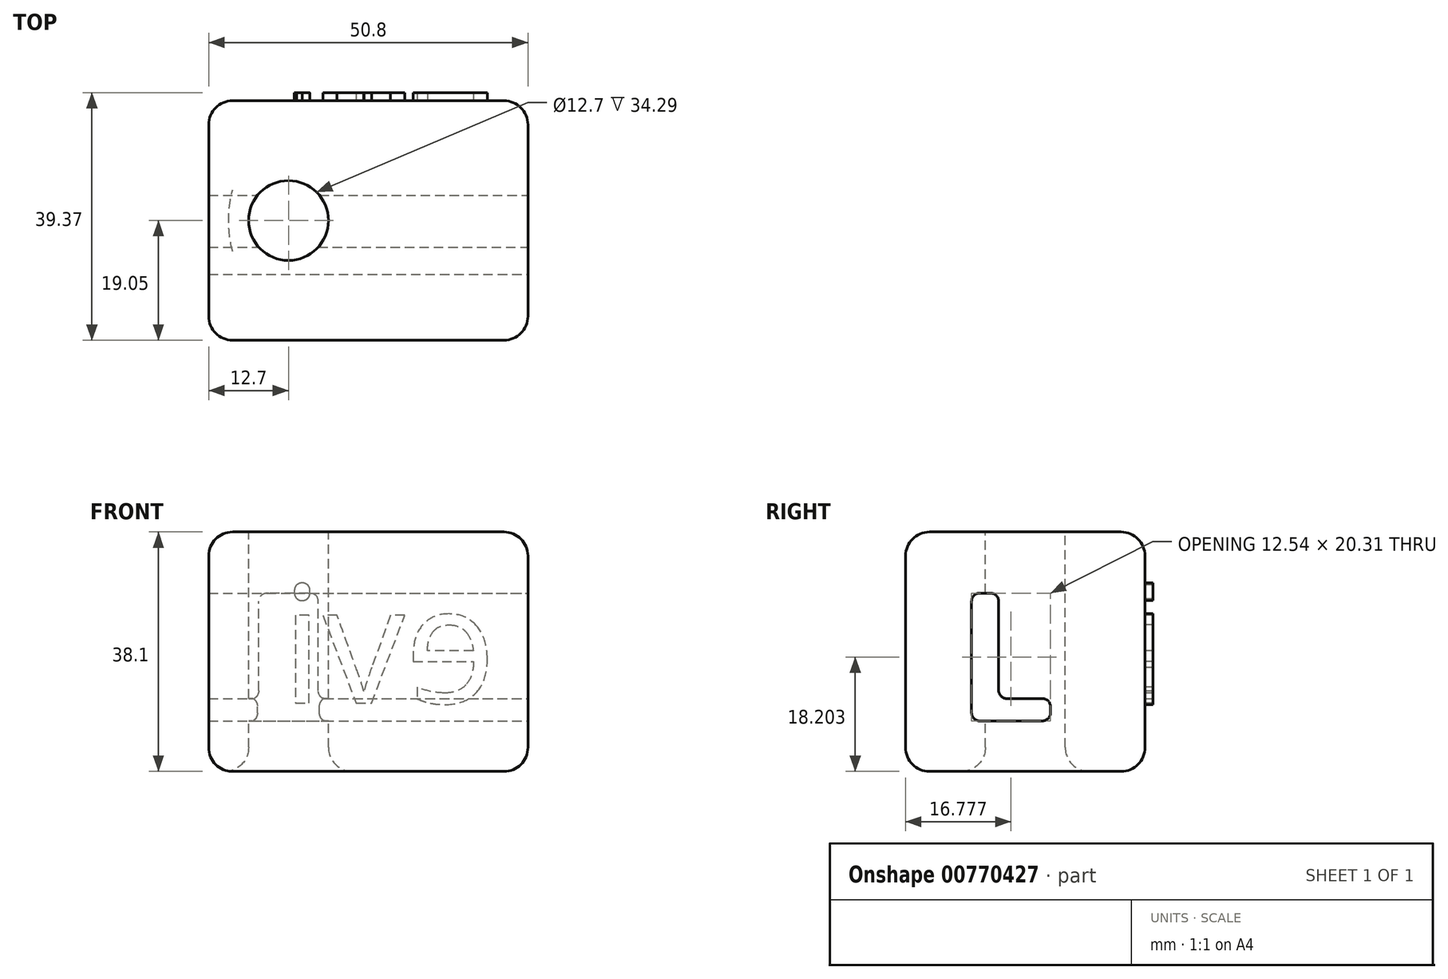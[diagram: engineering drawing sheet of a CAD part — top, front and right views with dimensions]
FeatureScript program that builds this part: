
annotation { "Feature Type Name" : "Feature", "Feature Type Description" : "" }
export const myFeature = defineFeature(function(context is Context, id is Id, definition is map)
    precondition{}
    {
        {
            var Q0;
            Q0=qCreatedBy(makeId("Top.planeOp"),FACE);
            var sketch = newSketch(context, id + "F0", { "sketchPlane" : qUnion([Q0])});
            skLineSegment(sketch, "E0.bottom", {"start": v(0, 0) * mm, "end": v(50.8, 0) * mm});
            skLineSegment(sketch, "E0.top", {"start": v(0, 38.1) * mm, "end": v(50.8, 38.1) * mm});
            skLineSegment(sketch, "E0.left", {"start": v(0, 0) * mm, "end": v(0, 38.1) * mm});
            skLineSegment(sketch, "E0.right", {"start": v(50.8, 0) * mm, "end": v(50.8, 38.1) * mm});
            skSolve(sketch);
        }
        {
            var Q0;
            Q0 = qSketchRegion(id + "F0", true);
            extrude(context, id + "F1", {"entities" : qUnion([Q0]), "depth" : 38.1 * mm, "offsetDistance" : 25.4 * mm});
        }
        {
            var Q0;
            Q0=makeQuery(id+"F1.opExtrude","CAP_FACE",FACE,{"disambiguationData":[OSD([sQuery(id+"F0.wireOp",EDGE,"E0.bottom"),sQuery(id+"F0.wireOp",EDGE,"E0.top"),sQuery(id+"F0.wireOp",EDGE,"E0.left"),sQuery(id+"F0.wireOp",EDGE,"E0.right")])],"isStart":false});
            var sketch = newSketch(context, id + "F2", { "sketchPlane" : qUnion([Q0])});
            skCircle(sketch, "E1", {"center": v(12.7, 19.05) * mm, "radius": 6.35 * mm});
            skSolve(sketch);
        }
        {
            var Q0;
            Q0 = qSketchRegion(id + "F2", true);
            extrude(context, id + "F3", {"entities" : qUnion([Q0]), "operationType" : NewBodyOperationType.REMOVE, "endBound" : BoundingType.THROUGH_ALL, "oppositeDirection" : true, "depth" : 25.4 * mm, "offsetDistance" : 25.4 * mm});
        }
        {
            var Q0;
            Q0=makeQuery(id+"F1.opExtrude","CAP_EDGE",EDGE,{"disambiguationData":[OSD([sQuery(id+"F0.wireOp",EDGE,"E0.bottom")])],"isStart":false});
            var Q1;
            Q1=makeQuery(id+"F1.opExtrude","CAP_EDGE",EDGE,{"disambiguationData":[OSD([sQuery(id+"F0.wireOp",EDGE,"E0.left")])],"isStart":false});
            var Q2;
            Q2=makeQuery(id+"F1.opExtrude","CAP_EDGE",EDGE,{"disambiguationData":[OSD([sQuery(id+"F0.wireOp",EDGE,"E0.top")])],"isStart":false});
            var Q3;
            Q3=makeQuery(id+"F1.opExtrude","CAP_EDGE",EDGE,{"disambiguationData":[OSD([sQuery(id+"F0.wireOp",EDGE,"E0.right")])],"isStart":false});
            var Q4;
            Q4=makeQuery(id+"F1.opExtrude","CAP_EDGE",EDGE,{"disambiguationData":[OSD([sQuery(id+"F0.wireOp",EDGE,"E0.top")])],"isStart":true});
            var Q5;
            Q5=makeQuery(id+"F1.opExtrude","CAP_EDGE",EDGE,{"disambiguationData":[OSD([sQuery(id+"F0.wireOp",EDGE,"E0.left")])],"isStart":true});
            var Q6;
            Q6=makeQuery(id+"F1.opExtrude","CAP_EDGE",EDGE,{"disambiguationData":[OSD([sQuery(id+"F0.wireOp",EDGE,"E0.bottom")])],"isStart":true});
            var Q7;
            Q7=makeQuery(id+"F1.opExtrude","CAP_FACE",FACE,{"disambiguationData":[OSD([sQuery(id+"F0.wireOp",EDGE,"E0.bottom"),sQuery(id+"F0.wireOp",EDGE,"E0.top"),sQuery(id+"F0.wireOp",EDGE,"E0.left"),sQuery(id+"F0.wireOp",EDGE,"E0.right")])],"isStart":true});
            var Q8;
            Q8=makeQuery(id+"F3.boolean.opBoolean","COPY",EDGE,{"derivedFrom":makeQuery(id+"F3.opExtrude","CAP_EDGE",EDGE,{"disambiguationData":[OSD([sQuery(id+"F2.wireOp",EDGE,"E1")])],"isStart":true})});
            var Q9;
            Q9=makeQuery(id+"F1.opExtrude","SWEPT_EDGE",EDGE,{"disambiguationData":[OSD([sQuery(id+"F0.wireOp",EDGE,"E0.bottom"),sQuery(id+"F0.wireOp",EDGE,"E0.right")])]});
            var Q10;
            Q10=makeQuery(id+"F1.opExtrude","SWEPT_EDGE",EDGE,{"disambiguationData":[OSD([sQuery(id+"F0.wireOp",EDGE,"E0.top"),sQuery(id+"F0.wireOp",EDGE,"E0.right")])]});
            var Q11;
            Q11=makeQuery(id+"F1.opExtrude","SWEPT_EDGE",EDGE,{"disambiguationData":[OSD([sQuery(id+"F0.wireOp",EDGE,"E0.top"),sQuery(id+"F0.wireOp",EDGE,"E0.left")])]});
            var Q12;
            Q12=makeQuery(id+"F1.opExtrude","SWEPT_EDGE",EDGE,{"disambiguationData":[OSD([sQuery(id+"F0.wireOp",EDGE,"E0.bottom"),sQuery(id+"F0.wireOp",EDGE,"E0.left")])]});
            fillet(context, id + "F4", {"entities" : qUnion([Q0, Q1, Q2, Q3, Q4, Q5, Q6, Q7, Q8, Q9, Q10, Q11, Q12]), "radius" : 3.8 * mm, "tangentPropagation" : true, "allowEdgeOverflow" : false});
        }
        {
            var Q0;
            Q0=makeQuery(id+"F1.opExtrude","SWEPT_FACE",FACE,{"disambiguationData":[OSD([sQuery(id+"F0.wireOp",EDGE,"E0.right")])]});
            var sketch = newSketch(context, id + "F5", { "sketchPlane" : qUnion([Q0])});
            skText(sketch, "E2", { "text": "L", "fontName": "OpenSans-Bold.ttf"});
            const initialGuessF5  = {"E2": [0.00795, 0.00805, 1, 0, 0.02048]};
            skSetInitialGuess(sketch, initialGuessF5);
            skSolve(sketch);
        }
        {
            var Q0;
            Q0 = qSketchRegion(id + "F5", true);
            extrude(context, id + "F6", {"entities" : qUnion([Q0]), "operationType" : NewBodyOperationType.REMOVE, "endBound" : BoundingType.THROUGH_ALL, "oppositeDirection" : true, "depth" : 6.35 * mm, "offsetDistance" : 25.4 * mm});
        }
        {
            var Q0;
            Q0=makeQuery(id+"F6.boolean.opBoolean","COPY",EDGE,{"derivedFrom":makeQuery(id+"F6.opExtrude","SWEPT_EDGE",EDGE,{"disambiguationData":[OSD([sQuery(id+"F5.wireOp",EDGE,"E2.sketch_text.stroke-0"),sQuery(id+"F5.wireOp",EDGE,"E2.sketch_text.stroke-1")])]})});
            var Q1;
            {var subQ0=sQuery(id+"F5.wireOp",EDGE,"E2.sketch_text.stroke-1");var subQ1=sQuery(id+"F5.wireOp",EDGE,"E2.sketch_text.stroke-2");Q1=makeQuery(id+"F6.boolean.opBoolean","COPY",EDGE,{"disambiguationData":[TD([makeQuery(id+"F1.opExtrude","SWEPT_FACE",FACE,{"disambiguationData":[OSD([sQuery(id+"F0.wireOp",EDGE,"E0.right")])]})])],"derivedFrom":makeQuery(id+"F6.opExtrude","SWEPT_EDGE",EDGE,{"disambiguationData":[OSD([subQ0,subQ1])]})});}
            var Q2;
            {var subQ0=sQuery(id+"F5.wireOp",EDGE,"E2.sketch_text.stroke-2");var subQ1=sQuery(id+"F5.wireOp",EDGE,"E2.sketch_text.stroke-3");Q2=makeQuery(id+"F6.boolean.opBoolean","COPY",EDGE,{"disambiguationData":[TD([makeQuery(id+"F1.opExtrude","SWEPT_FACE",FACE,{"disambiguationData":[OSD([sQuery(id+"F0.wireOp",EDGE,"E0.right")])]})])],"derivedFrom":makeQuery(id+"F6.opExtrude","SWEPT_EDGE",EDGE,{"disambiguationData":[OSD([subQ0,subQ1])]})});}
            var Q3;
            {var subQ0=sQuery(id+"F5.wireOp",EDGE,"E2.sketch_text.stroke-4");var subQ1=sQuery(id+"F5.wireOp",EDGE,"E2.sketch_text.stroke-3");Q3=makeQuery(id+"F6.boolean.opBoolean","COPY",EDGE,{"disambiguationData":[TD([makeQuery(id+"F1.opExtrude","SWEPT_FACE",FACE,{"disambiguationData":[OSD([sQuery(id+"F0.wireOp",EDGE,"E0.right")])]})])],"derivedFrom":makeQuery(id+"F6.opExtrude","SWEPT_EDGE",EDGE,{"disambiguationData":[OSD([subQ1,subQ0])]})});}
            var Q4;
            {var subQ0=sQuery(id+"F5.wireOp",EDGE,"E2.sketch_text.stroke-5");var subQ1=sQuery(id+"F5.wireOp",EDGE,"E2.sketch_text.stroke-4");Q4=makeQuery(id+"F6.boolean.opBoolean","COPY",EDGE,{"disambiguationData":[TD([makeQuery(id+"F1.opExtrude","SWEPT_FACE",FACE,{"disambiguationData":[OSD([sQuery(id+"F0.wireOp",EDGE,"E0.right")])]})])],"derivedFrom":makeQuery(id+"F6.opExtrude","SWEPT_EDGE",EDGE,{"disambiguationData":[OSD([subQ1,subQ0])]})});}
            var Q5;
            Q5=makeQuery(id+"F6.boolean.opBoolean","COPY",EDGE,{"derivedFrom":makeQuery(id+"F6.opExtrude","SWEPT_EDGE",EDGE,{"disambiguationData":[OSD([sQuery(id+"F5.wireOp",EDGE,"E2.sketch_text.stroke-0"),sQuery(id+"F5.wireOp",EDGE,"E2.sketch_text.stroke-5")])]})});
            var Q6;
            {var subQ0=sQuery(id+"F5.wireOp",EDGE,"E2.sketch_text.stroke-1");var subQ1=sQuery(id+"F5.wireOp",EDGE,"E2.sketch_text.stroke-2");Q6=makeQuery(id+"F6.boolean.opBoolean","COPY",EDGE,{"disambiguationData":[TD([makeQuery(id+"F1.opExtrude","SWEPT_FACE",FACE,{"disambiguationData":[OSD([sQuery(id+"F0.wireOp",EDGE,"E0.left")])]})])],"derivedFrom":makeQuery(id+"F6.opExtrude","SWEPT_EDGE",EDGE,{"disambiguationData":[OSD([subQ0,subQ1])]})});}
            var Q7;
            {var subQ0=sQuery(id+"F5.wireOp",EDGE,"E2.sketch_text.stroke-2");var subQ1=sQuery(id+"F5.wireOp",EDGE,"E2.sketch_text.stroke-3");Q7=makeQuery(id+"F6.boolean.opBoolean","COPY",EDGE,{"disambiguationData":[TD([makeQuery(id+"F1.opExtrude","SWEPT_FACE",FACE,{"disambiguationData":[OSD([sQuery(id+"F0.wireOp",EDGE,"E0.left")])]})])],"derivedFrom":makeQuery(id+"F6.opExtrude","SWEPT_EDGE",EDGE,{"disambiguationData":[OSD([subQ0,subQ1])]})});}
            var Q8;
            {var subQ0=sQuery(id+"F5.wireOp",EDGE,"E2.sketch_text.stroke-4");var subQ1=sQuery(id+"F5.wireOp",EDGE,"E2.sketch_text.stroke-3");Q8=makeQuery(id+"F6.boolean.opBoolean","COPY",EDGE,{"disambiguationData":[TD([makeQuery(id+"F1.opExtrude","SWEPT_FACE",FACE,{"disambiguationData":[OSD([sQuery(id+"F0.wireOp",EDGE,"E0.left")])]})])],"derivedFrom":makeQuery(id+"F6.opExtrude","SWEPT_EDGE",EDGE,{"disambiguationData":[OSD([subQ1,subQ0])]})});}
            var Q9;
            {var subQ0=sQuery(id+"F5.wireOp",EDGE,"E2.sketch_text.stroke-4");var subQ1=sQuery(id+"F5.wireOp",EDGE,"E2.sketch_text.stroke-5");Q9=makeQuery(id+"F6.boolean.opBoolean","COPY",EDGE,{"disambiguationData":[TD([makeQuery(id+"F1.opExtrude","SWEPT_FACE",FACE,{"disambiguationData":[OSD([sQuery(id+"F0.wireOp",EDGE,"E0.left")])]})])],"derivedFrom":makeQuery(id+"F6.opExtrude","SWEPT_EDGE",EDGE,{"disambiguationData":[OSD([subQ0,subQ1])]})});}
            fillet(context, id + "F7", {"entities" : qUnion([Q0, Q1, Q2, Q3, Q4, Q5, Q6, Q7, Q8, Q9]), "radius" : 1.27 * mm, "tangentPropagation" : true, "allowEdgeOverflow" : false});
        }
        {
            var Q0;
            Q0=makeQuery(id+"F1.opExtrude","SWEPT_FACE",FACE,{"disambiguationData":[OSD([sQuery(id+"F0.wireOp",EDGE,"E0.top")])]});
            var sketch = newSketch(context, id + "F8", { "sketchPlane" : qUnion([Q0])});
            skText(sketch, "E3", { "text": "evi", "fontName": "OpenSans-Regular.ttf"});
            const initialGuessF8  = {"E3": [-0.0458, 0.0109, 1, 0, 0.01873]};
            skSetInitialGuess(sketch, initialGuessF8);
            skSolve(sketch);
        }
        {
            var Q0;
            Q0 = qSketchRegion(id + "F8", true);
            extrude(context, id + "F9", {"entities" : qUnion([Q0]), "operationType" : NewBodyOperationType.ADD, "depth" : 1.27 * mm, "offsetDistance" : 25.4 * mm});
        }
    });
